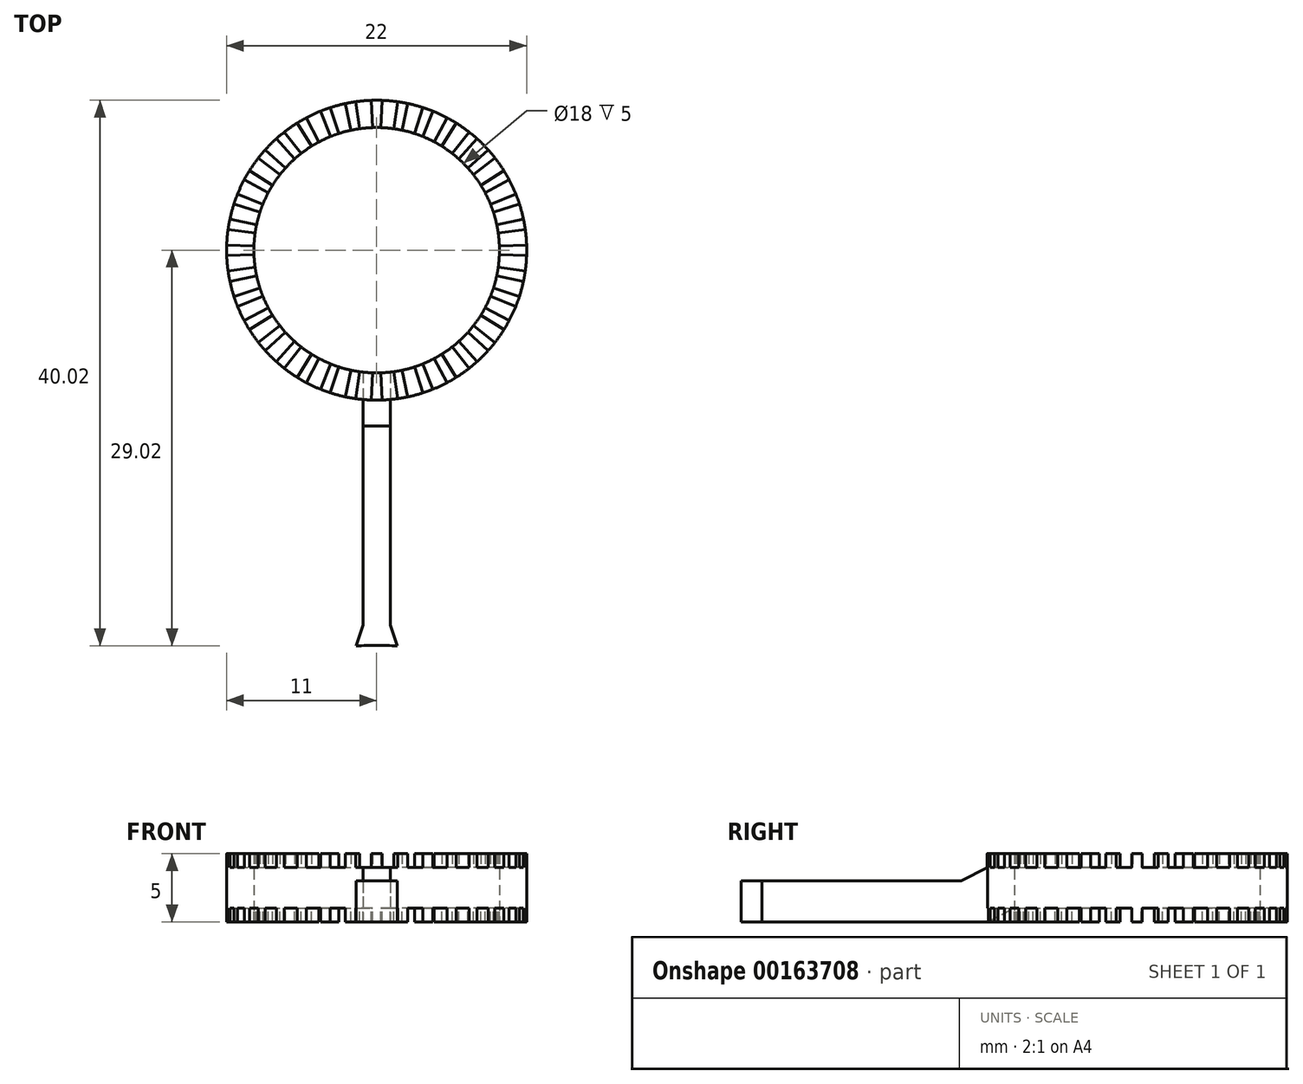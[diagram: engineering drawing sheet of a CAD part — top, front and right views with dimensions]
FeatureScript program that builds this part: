
annotation { "Feature Type Name" : "Feature", "Feature Type Description" : "" }
export const myFeature = defineFeature(function(context is Context, id is Id, definition is map)
    precondition{}
    {
        {
            var Q0;
            Q0=qCreatedBy(makeId("Top.planeOp"),FACE);
            cPlane(context, id + "F0", {"entities" : qUnion([Q0]), "cplaneType" : CPlaneType.OFFSET, "offset" : 1 * mm, "width" : 150 * mm, "height" : 150 * mm});
        }
        {
            var Q0;
            Q0=qCreatedBy(makeId("Top.planeOp"),FACE);
            var sketch = newSketch(context, id + "F1", { "sketchPlane" : qUnion([Q0])});
            skLineSegment(sketch, "E0", {"start": v(-1.5, -20.02) * mm, "end": v(-1, -18.51) * mm});
            skLineSegment(sketch, "E1", {"start": v(-1, -18.51) * mm, "end": v(-1, -1.95) * mm});
            skArc(sketch, "E2", {"start": v(1.5, -20.02) * mm, "mid": v(0, -20) * mm, "end": v(-1.5, -20.02) * mm});
            skLineSegment(sketch, "E3", {"start": v(0, 20) * mm, "end": v(0, -20) * mm, "construction": true});
            skLineSegment(sketch, "E4.MirrorCS", {"start": v(1, -18.51) * mm, "end": v(1, -1.95) * mm});
            skLineSegment(sketch, "E5.MirrorCS", {"start": v(1.5, -20.02) * mm, "end": v(1, -18.51) * mm});
            skLineSegment(sketch, "E6", {"start": v(-1, -1.95) * mm, "end": v(1, -1.95) * mm});
            skSolve(sketch);
        }
        {
            var Q0;
            Q0=qSketchRegion(id+"F1",true);
            extrude(context, id + "F2", {"entities" : qUnion([Q0]), "depth" : 3 * mm});
        }
        {
            var Q0;
            Q0=qCreatedBy(id+"F0.planeOp",FACE);
            var sketch = newSketch(context, id + "F3", { "sketchPlane" : qUnion([Q0])});
            skCircle(sketch, "E7", {"center": v(0, 9) * mm, "radius": 11 * mm});
            skCircle(sketch, "E8", {"center": v(0, 9) * mm, "radius": 9 * mm});
            skSolve(sketch);
        }
        {
            var Q0;
            Q0=qSketchRegion(id+"F3",true);
            extrude(context, id + "F4", {"entities" : qUnion([Q0]), "operationType" : NewBodyOperationType.ADD, "depth" : 3 * mm});
        }
        {
            var Q0;
            Q0=qCreatedBy(makeId("Right.planeOp"),FACE);
            var sketch = newSketch(context, id + "F5", { "sketchPlane" : qUnion([Q0])});
            skLineSegment(sketch, "E9", {"start": v(-1.95, 4) * mm, "end": v(-3.9, 3) * mm});
            skLineSegment(sketch, "E10", {"start": v(-3.9, 3) * mm, "end": v(-1.95, 3) * mm});
            skLineSegment(sketch, "E11", {"start": v(-1.95, 3) * mm, "end": v(-1.95, 4) * mm});
            skLineSegment(sketch, "E12", {"start": v(-1.95, 1) * mm, "end": v(-1.95, 0) * mm});
            skLineSegment(sketch, "E13", {"start": v(-1.95, 0) * mm, "end": v(0, 1) * mm});
            skLineSegment(sketch, "E14", {"start": v(0, 1) * mm, "end": v(-1.95, 1) * mm});
            skLineSegment(sketch, "E15", {"start": v(9, 1) * mm, "end": v(0, 1) * mm, "construction": true});
            skSolve(sketch);
        }
        {
            var Q0;
            Q0=qSketchRegion(id+"F5",true);
            extrude(context, id + "F6", {"entities" : qUnion([Q0]), "operationType" : NewBodyOperationType.ADD, "endBound" : BoundingType.SYMMETRIC, "depth" : 2 * mm});
        }
        {
            var Q0;
            Q0=makeQuery(id+"F4.opExtrude","CAP_FACE",FACE,{"disambiguationData":[OSD([sQuery(id+"F3.wireOp",EDGE,"E7"),sQuery(id+"F3.wireOp",EDGE,"E8")])],"isStart":false});
            var sketch = newSketch(context, id + "F7", { "sketchPlane" : qUnion([Q0])});
            skLineSegment(sketch, "E16", {"start": v(0, 9) * mm, "end": v(0, 20.9) * mm, "construction": true});
            skPoint(sketch, "E16.endSnap0", {"position": v(0, 20) * mm});
            skLineSegment(sketch, "E17", {"start": v(-0.38, 20) * mm, "end": v(-0.31, 18) * mm});
            skArc(sketch, "E18", {"start": v(-0.31, 18) * mm, "mid": v(-0.16, 18) * mm, "end": v(0, 18) * mm});
            skArc(sketch, "E19", {"start": v(-0.38, 20) * mm, "mid": v(-0.2, 20) * mm, "end": v(0, 20) * mm});
            skArc(sketch, "E20.MirrorCS", {"start": v(0.38, 20) * mm, "mid": v(0.2, 20) * mm, "end": v(0, 20) * mm});
            skLineSegment(sketch, "E21.MirrorCS", {"start": v(0.38, 20) * mm, "end": v(0.31, 18) * mm});
            skArc(sketch, "E22.MirrorCS", {"start": v(0.31, 18) * mm, "mid": v(0.16, 18) * mm, "end": v(0, 18) * mm});
            skLineSegment(sketch, "E23.1.0", {"start": v(-2.29, 19.76) * mm, "end": v(-1.87, 17.8) * mm});
            skArc(sketch, "E23.1.1", {"start": v(-2.29, 19.76) * mm, "mid": v(-2.1, 19.8) * mm, "end": v(-1.91, 19.83) * mm});
            skArc(sketch, "E23.1.2", {"start": v(-1.53, 19.9) * mm, "mid": v(-1.72, 19.86) * mm, "end": v(-1.91, 19.83) * mm});
            skLineSegment(sketch, "E23.1.3", {"start": v(-1.53, 19.9) * mm, "end": v(-1.25, 17.91) * mm});
            skArc(sketch, "E23.1.4", {"start": v(-1.25, 17.91) * mm, "mid": v(-1.4, 17.89) * mm, "end": v(-1.56, 17.86) * mm});
            skArc(sketch, "E23.1.5", {"start": v(-1.87, 17.8) * mm, "mid": v(-1.72, 17.83) * mm, "end": v(-1.56, 17.86) * mm});
            skLineSegment(sketch, "E23.2.0", {"start": v(-4.12, 19.2) * mm, "end": v(-3.37, 17.34) * mm});
            skArc(sketch, "E23.2.1", {"start": v(-4.12, 19.2) * mm, "mid": v(-3.94, 19.27) * mm, "end": v(-3.76, 19.34) * mm});
            skArc(sketch, "E23.2.2", {"start": v(-3.4, 19.46) * mm, "mid": v(-3.58, 19.4) * mm, "end": v(-3.76, 19.34) * mm});
            skLineSegment(sketch, "E23.2.3", {"start": v(-3.4, 19.46) * mm, "end": v(-2.78, 17.56) * mm});
            skArc(sketch, "E23.2.4", {"start": v(-2.78, 17.56) * mm, "mid": v(-2.93, 17.5) * mm, "end": v(-3.08, 17.46) * mm});
            skArc(sketch, "E23.2.5", {"start": v(-3.37, 17.34) * mm, "mid": v(-3.23, 17.4) * mm, "end": v(-3.08, 17.46) * mm});
            skLineSegment(sketch, "E23.3.0", {"start": v(-5.83, 18.33) * mm, "end": v(-4.77, 16.63) * mm});
            skArc(sketch, "E23.3.1", {"start": v(-5.83, 18.33) * mm, "mid": v(-5.67, 18.43) * mm, "end": v(-5.5, 18.53) * mm});
            skArc(sketch, "E23.3.2", {"start": v(-5.16, 18.71) * mm, "mid": v(-5.33, 18.62) * mm, "end": v(-5.5, 18.53) * mm});
            skLineSegment(sketch, "E23.3.3", {"start": v(-5.16, 18.71) * mm, "end": v(-4.23, 16.95) * mm});
            skArc(sketch, "E23.3.4", {"start": v(-4.23, 16.95) * mm, "mid": v(-4.36, 16.87) * mm, "end": v(-4.5, 16.8) * mm});
            skArc(sketch, "E23.3.5", {"start": v(-4.77, 16.63) * mm, "mid": v(-4.64, 16.71) * mm, "end": v(-4.5, 16.8) * mm});
            skLineSegment(sketch, "E23.4.0", {"start": v(-7.36, 17.17) * mm, "end": v(-6.02, 15.69) * mm});
            skArc(sketch, "E23.4.1", {"start": v(-7.36, 17.17) * mm, "mid": v(-7.22, 17.3) * mm, "end": v(-7.07, 17.43) * mm});
            skArc(sketch, "E23.4.2", {"start": v(-6.77, 17.67) * mm, "mid": v(-6.92, 17.55) * mm, "end": v(-7.07, 17.43) * mm});
            skLineSegment(sketch, "E23.4.3", {"start": v(-6.77, 17.67) * mm, "end": v(-5.54, 16.1) * mm});
            skArc(sketch, "E23.4.4", {"start": v(-5.54, 16.1) * mm, "mid": v(-5.66, 16) * mm, "end": v(-5.79, 15.9) * mm});
            skArc(sketch, "E23.4.5", {"start": v(-6.02, 15.69) * mm, "mid": v(-5.9, 15.8) * mm, "end": v(-5.79, 15.9) * mm});
            skLineSegment(sketch, "E23.5.0", {"start": v(-8.67, 15.77) * mm, "end": v(-7.1, 14.54) * mm});
            skArc(sketch, "E23.5.1", {"start": v(-8.67, 15.77) * mm, "mid": v(-8.55, 15.92) * mm, "end": v(-8.43, 16.07) * mm});
            skArc(sketch, "E23.5.2", {"start": v(-8.17, 16.36) * mm, "mid": v(-8.3, 16.22) * mm, "end": v(-8.43, 16.07) * mm});
            skLineSegment(sketch, "E23.5.3", {"start": v(-8.17, 16.36) * mm, "end": v(-6.69, 15.02) * mm});
            skArc(sketch, "E23.5.4", {"start": v(-6.69, 15.02) * mm, "mid": v(-6.8, 14.9) * mm, "end": v(-6.9, 14.79) * mm});
            skArc(sketch, "E23.5.5", {"start": v(-7.1, 14.54) * mm, "mid": v(-7, 14.66) * mm, "end": v(-6.9, 14.79) * mm});
            skLineSegment(sketch, "E23.6.0", {"start": v(-9.71, 14.16) * mm, "end": v(-7.95, 13.23) * mm});
            skArc(sketch, "E23.6.1", {"start": v(-9.71, 14.16) * mm, "mid": v(-9.62, 14.33) * mm, "end": v(-9.53, 14.5) * mm});
            skArc(sketch, "E23.6.2", {"start": v(-9.33, 14.83) * mm, "mid": v(-9.43, 14.67) * mm, "end": v(-9.53, 14.5) * mm});
            skLineSegment(sketch, "E23.6.3", {"start": v(-9.33, 14.83) * mm, "end": v(-7.63, 13.77) * mm});
            skArc(sketch, "E23.6.4", {"start": v(-7.63, 13.77) * mm, "mid": v(-7.71, 13.64) * mm, "end": v(-7.8, 13.5) * mm});
            skArc(sketch, "E23.6.5", {"start": v(-7.95, 13.23) * mm, "mid": v(-7.87, 13.36) * mm, "end": v(-7.8, 13.5) * mm});
            skLineSegment(sketch, "E23.7.0", {"start": v(-10.46, 12.4) * mm, "end": v(-8.56, 11.78) * mm});
            skArc(sketch, "E23.7.1", {"start": v(-10.46, 12.4) * mm, "mid": v(-10.4, 12.58) * mm, "end": v(-10.34, 12.76) * mm});
            skArc(sketch, "E23.7.2", {"start": v(-10.2, 13.12) * mm, "mid": v(-10.27, 12.94) * mm, "end": v(-10.34, 12.76) * mm});
            skLineSegment(sketch, "E23.7.3", {"start": v(-10.2, 13.12) * mm, "end": v(-8.34, 12.37) * mm});
            skArc(sketch, "E23.7.4", {"start": v(-8.34, 12.37) * mm, "mid": v(-8.4, 12.23) * mm, "end": v(-8.46, 12.08) * mm});
            skArc(sketch, "E23.7.5", {"start": v(-8.56, 11.78) * mm, "mid": v(-8.5, 11.93) * mm, "end": v(-8.46, 12.08) * mm});
            skLineSegment(sketch, "E23.8.0", {"start": v(-10.9, 10.53) * mm, "end": v(-8.91, 10.25) * mm});
            skArc(sketch, "E23.8.1", {"start": v(-10.9, 10.53) * mm, "mid": v(-10.86, 10.72) * mm, "end": v(-10.83, 10.91) * mm});
            skArc(sketch, "E23.8.2", {"start": v(-10.76, 11.29) * mm, "mid": v(-10.8, 11.1) * mm, "end": v(-10.83, 10.91) * mm});
            skLineSegment(sketch, "E23.8.3", {"start": v(-10.76, 11.29) * mm, "end": v(-8.8, 10.87) * mm});
            skArc(sketch, "E23.8.4", {"start": v(-8.8, 10.87) * mm, "mid": v(-8.83, 10.72) * mm, "end": v(-8.86, 10.56) * mm});
            skArc(sketch, "E23.8.5", {"start": v(-8.91, 10.25) * mm, "mid": v(-8.89, 10.4) * mm, "end": v(-8.86, 10.56) * mm});
            skLineSegment(sketch, "E23.9.0", {"start": v(-11, 8.62) * mm, "end": v(-9, 8.69) * mm});
            skArc(sketch, "E23.9.1", {"start": v(-11, 8.62) * mm, "mid": v(-11, 8.8) * mm, "end": v(-11, 9) * mm});
            skArc(sketch, "E23.9.2", {"start": v(-11, 9.38) * mm, "mid": v(-11, 9.2) * mm, "end": v(-11, 9) * mm});
            skLineSegment(sketch, "E23.9.3", {"start": v(-11, 9.38) * mm, "end": v(-9, 9.31) * mm});
            skArc(sketch, "E23.9.4", {"start": v(-9, 9.31) * mm, "mid": v(-9, 9.16) * mm, "end": v(-9, 9) * mm});
            skArc(sketch, "E23.9.5", {"start": v(-9, 8.69) * mm, "mid": v(-9, 8.84) * mm, "end": v(-9, 9) * mm});
            skLineSegment(sketch, "E23.10.0", {"start": v(-10.76, 6.71) * mm, "end": v(-8.8, 7.13) * mm});
            skArc(sketch, "E23.10.1", {"start": v(-10.76, 6.71) * mm, "mid": v(-10.8, 6.9) * mm, "end": v(-10.83, 7.09) * mm});
            skArc(sketch, "E23.10.2", {"start": v(-10.9, 7.47) * mm, "mid": v(-10.86, 7.28) * mm, "end": v(-10.83, 7.09) * mm});
            skLineSegment(sketch, "E23.10.3", {"start": v(-10.9, 7.47) * mm, "end": v(-8.91, 7.75) * mm});
            skArc(sketch, "E23.10.4", {"start": v(-8.91, 7.75) * mm, "mid": v(-8.89, 7.6) * mm, "end": v(-8.86, 7.44) * mm});
            skArc(sketch, "E23.10.5", {"start": v(-8.8, 7.13) * mm, "mid": v(-8.83, 7.28) * mm, "end": v(-8.86, 7.44) * mm});
            skLineSegment(sketch, "E23.11.0", {"start": v(-10.2, 4.88) * mm, "end": v(-8.34, 5.63) * mm});
            skArc(sketch, "E23.11.1", {"start": v(-10.2, 4.88) * mm, "mid": v(-10.27, 5.06) * mm, "end": v(-10.34, 5.24) * mm});
            skArc(sketch, "E23.11.2", {"start": v(-10.46, 5.6) * mm, "mid": v(-10.4, 5.42) * mm, "end": v(-10.34, 5.24) * mm});
            skLineSegment(sketch, "E23.11.3", {"start": v(-10.46, 5.6) * mm, "end": v(-8.56, 6.22) * mm});
            skArc(sketch, "E23.11.4", {"start": v(-8.56, 6.22) * mm, "mid": v(-8.5, 6.07) * mm, "end": v(-8.46, 5.92) * mm});
            skArc(sketch, "E23.11.5", {"start": v(-8.34, 5.63) * mm, "mid": v(-8.4, 5.77) * mm, "end": v(-8.46, 5.92) * mm});
            skLineSegment(sketch, "E23.12.0", {"start": v(-9.33, 3.17) * mm, "end": v(-7.63, 4.23) * mm});
            skArc(sketch, "E23.12.1", {"start": v(-9.33, 3.17) * mm, "mid": v(-9.43, 3.33) * mm, "end": v(-9.53, 3.5) * mm});
            skArc(sketch, "E23.12.2", {"start": v(-9.71, 3.84) * mm, "mid": v(-9.62, 3.67) * mm, "end": v(-9.53, 3.5) * mm});
            skLineSegment(sketch, "E23.12.3", {"start": v(-9.71, 3.84) * mm, "end": v(-7.95, 4.77) * mm});
            skArc(sketch, "E23.12.4", {"start": v(-7.95, 4.77) * mm, "mid": v(-7.87, 4.64) * mm, "end": v(-7.8, 4.5) * mm});
            skArc(sketch, "E23.12.5", {"start": v(-7.63, 4.23) * mm, "mid": v(-7.71, 4.36) * mm, "end": v(-7.8, 4.5) * mm});
            skLineSegment(sketch, "E23.13.0", {"start": v(-8.17, 1.64) * mm, "end": v(-6.69, 2.98) * mm});
            skArc(sketch, "E23.13.1", {"start": v(-8.17, 1.64) * mm, "mid": v(-8.3, 1.78) * mm, "end": v(-8.43, 1.93) * mm});
            skArc(sketch, "E23.13.2", {"start": v(-8.67, 2.23) * mm, "mid": v(-8.55, 2.08) * mm, "end": v(-8.43, 1.93) * mm});
            skLineSegment(sketch, "E23.13.3", {"start": v(-8.67, 2.23) * mm, "end": v(-7.1, 3.46) * mm});
            skArc(sketch, "E23.13.4", {"start": v(-7.1, 3.46) * mm, "mid": v(-7, 3.34) * mm, "end": v(-6.9, 3.21) * mm});
            skArc(sketch, "E23.13.5", {"start": v(-6.69, 2.98) * mm, "mid": v(-6.8, 3.1) * mm, "end": v(-6.9, 3.21) * mm});
            skLineSegment(sketch, "E23.14.0", {"start": v(-6.77, 0.33) * mm, "end": v(-5.54, 1.9) * mm});
            skArc(sketch, "E23.14.1", {"start": v(-6.77, 0.33) * mm, "mid": v(-6.92, 0.45) * mm, "end": v(-7.07, 0.57) * mm});
            skArc(sketch, "E23.14.2", {"start": v(-7.36, 0.83) * mm, "mid": v(-7.22, 0.7) * mm, "end": v(-7.07, 0.57) * mm});
            skLineSegment(sketch, "E23.14.3", {"start": v(-7.36, 0.83) * mm, "end": v(-6.02, 2.31) * mm});
            skArc(sketch, "E23.14.4", {"start": v(-6.02, 2.31) * mm, "mid": v(-5.9, 2.2) * mm, "end": v(-5.79, 2.1) * mm});
            skArc(sketch, "E23.14.5", {"start": v(-5.54, 1.9) * mm, "mid": v(-5.66, 2) * mm, "end": v(-5.79, 2.1) * mm});
            skLineSegment(sketch, "E23.15.0", {"start": v(-5.16, -0.71) * mm, "end": v(-4.23, 1.05) * mm});
            skArc(sketch, "E23.15.1", {"start": v(-5.16, -0.71) * mm, "mid": v(-5.33, -0.62) * mm, "end": v(-5.5, -0.53) * mm});
            skArc(sketch, "E23.15.2", {"start": v(-5.83, -0.33) * mm, "mid": v(-5.67, -0.43) * mm, "end": v(-5.5, -0.53) * mm});
            skLineSegment(sketch, "E23.15.3", {"start": v(-5.83, -0.33) * mm, "end": v(-4.77, 1.37) * mm});
            skArc(sketch, "E23.15.4", {"start": v(-4.77, 1.37) * mm, "mid": v(-4.64, 1.29) * mm, "end": v(-4.5, 1.2) * mm});
            skArc(sketch, "E23.15.5", {"start": v(-4.23, 1.05) * mm, "mid": v(-4.36, 1.13) * mm, "end": v(-4.5, 1.2) * mm});
            skLineSegment(sketch, "E23.16.0", {"start": v(-3.4, -1.46) * mm, "end": v(-2.78, 0.44) * mm});
            skArc(sketch, "E23.16.1", {"start": v(-3.4, -1.46) * mm, "mid": v(-3.58, -1.4) * mm, "end": v(-3.76, -1.34) * mm});
            skArc(sketch, "E23.16.2", {"start": v(-4.12, -1.2) * mm, "mid": v(-3.94, -1.27) * mm, "end": v(-3.76, -1.34) * mm});
            skLineSegment(sketch, "E23.16.3", {"start": v(-4.12, -1.2) * mm, "end": v(-3.37, 0.66) * mm});
            skArc(sketch, "E23.16.4", {"start": v(-3.37, 0.66) * mm, "mid": v(-3.23, 0.6) * mm, "end": v(-3.08, 0.54) * mm});
            skArc(sketch, "E23.16.5", {"start": v(-2.78, 0.44) * mm, "mid": v(-2.93, 0.5) * mm, "end": v(-3.08, 0.54) * mm});
            skLineSegment(sketch, "E23.17.0", {"start": v(-1.53, -1.9) * mm, "end": v(-1.25, 0.09) * mm});
            skArc(sketch, "E23.17.1", {"start": v(-1.53, -1.9) * mm, "mid": v(-1.72, -1.86) * mm, "end": v(-1.91, -1.83) * mm});
            skArc(sketch, "E23.17.2", {"start": v(-2.29, -1.76) * mm, "mid": v(-2.1, -1.8) * mm, "end": v(-1.91, -1.83) * mm});
            skLineSegment(sketch, "E23.17.3", {"start": v(-2.29, -1.76) * mm, "end": v(-1.87, 0.2) * mm});
            skArc(sketch, "E23.17.4", {"start": v(-1.87, 0.2) * mm, "mid": v(-1.72, 0.17) * mm, "end": v(-1.56, 0.14) * mm});
            skArc(sketch, "E23.17.5", {"start": v(-1.25, 0.09) * mm, "mid": v(-1.4, 0.11) * mm, "end": v(-1.56, 0.14) * mm});
            skLineSegment(sketch, "E23.18.0", {"start": v(0.38, -2) * mm, "end": v(0.31, 0) * mm});
            skArc(sketch, "E23.18.1", {"start": v(0.38, -2) * mm, "mid": v(0.2, -2) * mm, "end": v(0, -2) * mm});
            skArc(sketch, "E23.18.2", {"start": v(-0.38, -2) * mm, "mid": v(-0.2, -2) * mm, "end": v(0, -2) * mm});
            skLineSegment(sketch, "E23.18.3", {"start": v(-0.38, -2) * mm, "end": v(-0.31, 0) * mm});
            skArc(sketch, "E23.18.4", {"start": v(-0.31, 0) * mm, "mid": v(-0.16, 0) * mm, "end": v(0, 0) * mm});
            skArc(sketch, "E23.18.5", {"start": v(0.31, 0) * mm, "mid": v(0.16, 0) * mm, "end": v(0, 0) * mm});
            skLineSegment(sketch, "E23.19.0", {"start": v(2.29, -1.76) * mm, "end": v(1.87, 0.2) * mm});
            skArc(sketch, "E23.19.1", {"start": v(2.29, -1.76) * mm, "mid": v(2.1, -1.8) * mm, "end": v(1.91, -1.83) * mm});
            skArc(sketch, "E23.19.2", {"start": v(1.53, -1.9) * mm, "mid": v(1.72, -1.86) * mm, "end": v(1.91, -1.83) * mm});
            skLineSegment(sketch, "E23.19.3", {"start": v(1.53, -1.9) * mm, "end": v(1.25, 0.09) * mm});
            skArc(sketch, "E23.19.4", {"start": v(1.25, 0.09) * mm, "mid": v(1.4, 0.11) * mm, "end": v(1.56, 0.14) * mm});
            skArc(sketch, "E23.19.5", {"start": v(1.87, 0.2) * mm, "mid": v(1.72, 0.17) * mm, "end": v(1.56, 0.14) * mm});
            skLineSegment(sketch, "E23.20.0", {"start": v(4.12, -1.2) * mm, "end": v(3.37, 0.66) * mm});
            skArc(sketch, "E23.20.1", {"start": v(4.12, -1.2) * mm, "mid": v(3.94, -1.27) * mm, "end": v(3.76, -1.34) * mm});
            skArc(sketch, "E23.20.2", {"start": v(3.4, -1.46) * mm, "mid": v(3.58, -1.4) * mm, "end": v(3.76, -1.34) * mm});
            skLineSegment(sketch, "E23.20.3", {"start": v(3.4, -1.46) * mm, "end": v(2.78, 0.44) * mm});
            skArc(sketch, "E23.20.4", {"start": v(2.78, 0.44) * mm, "mid": v(2.93, 0.5) * mm, "end": v(3.08, 0.54) * mm});
            skArc(sketch, "E23.20.5", {"start": v(3.37, 0.66) * mm, "mid": v(3.23, 0.6) * mm, "end": v(3.08, 0.54) * mm});
            skLineSegment(sketch, "E23.21.0", {"start": v(5.83, -0.33) * mm, "end": v(4.77, 1.37) * mm});
            skArc(sketch, "E23.21.1", {"start": v(5.83, -0.33) * mm, "mid": v(5.67, -0.43) * mm, "end": v(5.5, -0.53) * mm});
            skArc(sketch, "E23.21.2", {"start": v(5.16, -0.71) * mm, "mid": v(5.33, -0.62) * mm, "end": v(5.5, -0.53) * mm});
            skLineSegment(sketch, "E23.21.3", {"start": v(5.16, -0.71) * mm, "end": v(4.23, 1.05) * mm});
            skArc(sketch, "E23.21.4", {"start": v(4.23, 1.05) * mm, "mid": v(4.36, 1.13) * mm, "end": v(4.5, 1.2) * mm});
            skArc(sketch, "E23.21.5", {"start": v(4.77, 1.37) * mm, "mid": v(4.64, 1.29) * mm, "end": v(4.5, 1.2) * mm});
            skLineSegment(sketch, "E23.22.0", {"start": v(7.36, 0.83) * mm, "end": v(6.02, 2.31) * mm});
            skArc(sketch, "E23.22.1", {"start": v(7.36, 0.83) * mm, "mid": v(7.22, 0.7) * mm, "end": v(7.07, 0.57) * mm});
            skArc(sketch, "E23.22.2", {"start": v(6.77, 0.33) * mm, "mid": v(6.92, 0.45) * mm, "end": v(7.07, 0.57) * mm});
            skLineSegment(sketch, "E23.22.3", {"start": v(6.77, 0.33) * mm, "end": v(5.54, 1.9) * mm});
            skArc(sketch, "E23.22.4", {"start": v(5.54, 1.9) * mm, "mid": v(5.66, 2) * mm, "end": v(5.79, 2.1) * mm});
            skArc(sketch, "E23.22.5", {"start": v(6.02, 2.31) * mm, "mid": v(5.9, 2.2) * mm, "end": v(5.79, 2.1) * mm});
            skLineSegment(sketch, "E23.23.0", {"start": v(8.67, 2.23) * mm, "end": v(7.1, 3.46) * mm});
            skArc(sketch, "E23.23.1", {"start": v(8.67, 2.23) * mm, "mid": v(8.55, 2.08) * mm, "end": v(8.43, 1.93) * mm});
            skArc(sketch, "E23.23.2", {"start": v(8.17, 1.64) * mm, "mid": v(8.3, 1.78) * mm, "end": v(8.43, 1.93) * mm});
            skLineSegment(sketch, "E23.23.3", {"start": v(8.17, 1.64) * mm, "end": v(6.69, 2.98) * mm});
            skArc(sketch, "E23.23.4", {"start": v(6.69, 2.98) * mm, "mid": v(6.8, 3.1) * mm, "end": v(6.9, 3.21) * mm});
            skArc(sketch, "E23.23.5", {"start": v(7.1, 3.46) * mm, "mid": v(7, 3.34) * mm, "end": v(6.9, 3.21) * mm});
            skLineSegment(sketch, "E23.24.0", {"start": v(9.71, 3.84) * mm, "end": v(7.95, 4.77) * mm});
            skArc(sketch, "E23.24.1", {"start": v(9.71, 3.84) * mm, "mid": v(9.62, 3.67) * mm, "end": v(9.53, 3.5) * mm});
            skArc(sketch, "E23.24.2", {"start": v(9.33, 3.17) * mm, "mid": v(9.43, 3.33) * mm, "end": v(9.53, 3.5) * mm});
            skLineSegment(sketch, "E23.24.3", {"start": v(9.33, 3.17) * mm, "end": v(7.63, 4.23) * mm});
            skArc(sketch, "E23.24.4", {"start": v(7.63, 4.23) * mm, "mid": v(7.71, 4.36) * mm, "end": v(7.8, 4.5) * mm});
            skArc(sketch, "E23.24.5", {"start": v(7.95, 4.77) * mm, "mid": v(7.87, 4.64) * mm, "end": v(7.8, 4.5) * mm});
            skLineSegment(sketch, "E23.25.0", {"start": v(10.46, 5.6) * mm, "end": v(8.56, 6.22) * mm});
            skArc(sketch, "E23.25.1", {"start": v(10.46, 5.6) * mm, "mid": v(10.4, 5.42) * mm, "end": v(10.34, 5.24) * mm});
            skArc(sketch, "E23.25.2", {"start": v(10.2, 4.88) * mm, "mid": v(10.27, 5.06) * mm, "end": v(10.34, 5.24) * mm});
            skLineSegment(sketch, "E23.25.3", {"start": v(10.2, 4.88) * mm, "end": v(8.34, 5.63) * mm});
            skArc(sketch, "E23.25.4", {"start": v(8.34, 5.63) * mm, "mid": v(8.4, 5.77) * mm, "end": v(8.46, 5.92) * mm});
            skArc(sketch, "E23.25.5", {"start": v(8.56, 6.22) * mm, "mid": v(8.5, 6.07) * mm, "end": v(8.46, 5.92) * mm});
            skLineSegment(sketch, "E23.26.0", {"start": v(10.9, 7.47) * mm, "end": v(8.91, 7.75) * mm});
            skArc(sketch, "E23.26.1", {"start": v(10.9, 7.47) * mm, "mid": v(10.86, 7.28) * mm, "end": v(10.83, 7.09) * mm});
            skArc(sketch, "E23.26.2", {"start": v(10.76, 6.71) * mm, "mid": v(10.8, 6.9) * mm, "end": v(10.83, 7.09) * mm});
            skLineSegment(sketch, "E23.26.3", {"start": v(10.76, 6.71) * mm, "end": v(8.8, 7.13) * mm});
            skArc(sketch, "E23.26.4", {"start": v(8.8, 7.13) * mm, "mid": v(8.83, 7.28) * mm, "end": v(8.86, 7.44) * mm});
            skArc(sketch, "E23.26.5", {"start": v(8.91, 7.75) * mm, "mid": v(8.89, 7.6) * mm, "end": v(8.86, 7.44) * mm});
            skLineSegment(sketch, "E23.27.0", {"start": v(11, 9.38) * mm, "end": v(9, 9.31) * mm});
            skArc(sketch, "E23.27.1", {"start": v(11, 9.38) * mm, "mid": v(11, 9.2) * mm, "end": v(11, 9) * mm});
            skArc(sketch, "E23.27.2", {"start": v(11, 8.62) * mm, "mid": v(11, 8.8) * mm, "end": v(11, 9) * mm});
            skLineSegment(sketch, "E23.27.3", {"start": v(11, 8.62) * mm, "end": v(9, 8.69) * mm});
            skArc(sketch, "E23.27.4", {"start": v(9, 8.69) * mm, "mid": v(9, 8.84) * mm, "end": v(9, 9) * mm});
            skArc(sketch, "E23.27.5", {"start": v(9, 9.31) * mm, "mid": v(9, 9.16) * mm, "end": v(9, 9) * mm});
            skLineSegment(sketch, "E23.28.0", {"start": v(10.76, 11.29) * mm, "end": v(8.8, 10.87) * mm});
            skArc(sketch, "E23.28.1", {"start": v(10.76, 11.29) * mm, "mid": v(10.8, 11.1) * mm, "end": v(10.83, 10.91) * mm});
            skArc(sketch, "E23.28.2", {"start": v(10.9, 10.53) * mm, "mid": v(10.86, 10.72) * mm, "end": v(10.83, 10.91) * mm});
            skLineSegment(sketch, "E23.28.3", {"start": v(10.9, 10.53) * mm, "end": v(8.91, 10.25) * mm});
            skArc(sketch, "E23.28.4", {"start": v(8.91, 10.25) * mm, "mid": v(8.89, 10.4) * mm, "end": v(8.86, 10.56) * mm});
            skArc(sketch, "E23.28.5", {"start": v(8.8, 10.87) * mm, "mid": v(8.83, 10.72) * mm, "end": v(8.86, 10.56) * mm});
            skLineSegment(sketch, "E23.29.0", {"start": v(10.2, 13.12) * mm, "end": v(8.34, 12.37) * mm});
            skArc(sketch, "E23.29.1", {"start": v(10.2, 13.12) * mm, "mid": v(10.27, 12.94) * mm, "end": v(10.34, 12.76) * mm});
            skArc(sketch, "E23.29.2", {"start": v(10.46, 12.4) * mm, "mid": v(10.4, 12.58) * mm, "end": v(10.34, 12.76) * mm});
            skLineSegment(sketch, "E23.29.3", {"start": v(10.46, 12.4) * mm, "end": v(8.56, 11.78) * mm});
            skArc(sketch, "E23.29.4", {"start": v(8.56, 11.78) * mm, "mid": v(8.5, 11.93) * mm, "end": v(8.46, 12.08) * mm});
            skArc(sketch, "E23.29.5", {"start": v(8.34, 12.37) * mm, "mid": v(8.4, 12.23) * mm, "end": v(8.46, 12.08) * mm});
            skLineSegment(sketch, "E23.30.0", {"start": v(9.33, 14.83) * mm, "end": v(7.63, 13.77) * mm});
            skArc(sketch, "E23.30.1", {"start": v(9.33, 14.83) * mm, "mid": v(9.43, 14.67) * mm, "end": v(9.53, 14.5) * mm});
            skArc(sketch, "E23.30.2", {"start": v(9.71, 14.16) * mm, "mid": v(9.62, 14.33) * mm, "end": v(9.53, 14.5) * mm});
            skLineSegment(sketch, "E23.30.3", {"start": v(9.71, 14.16) * mm, "end": v(7.95, 13.23) * mm});
            skArc(sketch, "E23.30.4", {"start": v(7.95, 13.23) * mm, "mid": v(7.87, 13.36) * mm, "end": v(7.8, 13.5) * mm});
            skArc(sketch, "E23.30.5", {"start": v(7.63, 13.77) * mm, "mid": v(7.71, 13.64) * mm, "end": v(7.8, 13.5) * mm});
            skLineSegment(sketch, "E23.31.0", {"start": v(8.17, 16.36) * mm, "end": v(6.69, 15.02) * mm});
            skArc(sketch, "E23.31.1", {"start": v(8.17, 16.36) * mm, "mid": v(8.3, 16.22) * mm, "end": v(8.43, 16.07) * mm});
            skArc(sketch, "E23.31.2", {"start": v(8.67, 15.77) * mm, "mid": v(8.55, 15.92) * mm, "end": v(8.43, 16.07) * mm});
            skLineSegment(sketch, "E23.31.3", {"start": v(8.67, 15.77) * mm, "end": v(7.1, 14.54) * mm});
            skArc(sketch, "E23.31.4", {"start": v(7.1, 14.54) * mm, "mid": v(7, 14.66) * mm, "end": v(6.9, 14.79) * mm});
            skArc(sketch, "E23.31.5", {"start": v(6.69, 15.02) * mm, "mid": v(6.8, 14.9) * mm, "end": v(6.9, 14.79) * mm});
            skLineSegment(sketch, "E23.32.0", {"start": v(6.77, 17.67) * mm, "end": v(5.54, 16.1) * mm});
            skArc(sketch, "E23.32.1", {"start": v(6.77, 17.67) * mm, "mid": v(6.92, 17.55) * mm, "end": v(7.07, 17.43) * mm});
            skArc(sketch, "E23.32.2", {"start": v(7.36, 17.17) * mm, "mid": v(7.22, 17.3) * mm, "end": v(7.07, 17.43) * mm});
            skLineSegment(sketch, "E23.32.3", {"start": v(7.36, 17.17) * mm, "end": v(6.02, 15.69) * mm});
            skArc(sketch, "E23.32.4", {"start": v(6.02, 15.69) * mm, "mid": v(5.9, 15.8) * mm, "end": v(5.79, 15.9) * mm});
            skArc(sketch, "E23.32.5", {"start": v(5.54, 16.1) * mm, "mid": v(5.66, 16) * mm, "end": v(5.79, 15.9) * mm});
            skLineSegment(sketch, "E23.33.0", {"start": v(5.16, 18.71) * mm, "end": v(4.23, 16.95) * mm});
            skArc(sketch, "E23.33.1", {"start": v(5.16, 18.71) * mm, "mid": v(5.33, 18.62) * mm, "end": v(5.5, 18.53) * mm});
            skArc(sketch, "E23.33.2", {"start": v(5.83, 18.33) * mm, "mid": v(5.67, 18.43) * mm, "end": v(5.5, 18.53) * mm});
            skLineSegment(sketch, "E23.33.3", {"start": v(5.83, 18.33) * mm, "end": v(4.77, 16.63) * mm});
            skArc(sketch, "E23.33.4", {"start": v(4.77, 16.63) * mm, "mid": v(4.64, 16.71) * mm, "end": v(4.5, 16.8) * mm});
            skArc(sketch, "E23.33.5", {"start": v(4.23, 16.95) * mm, "mid": v(4.36, 16.87) * mm, "end": v(4.5, 16.8) * mm});
            skLineSegment(sketch, "E23.34.0", {"start": v(3.4, 19.46) * mm, "end": v(2.78, 17.56) * mm});
            skArc(sketch, "E23.34.1", {"start": v(3.4, 19.46) * mm, "mid": v(3.58, 19.4) * mm, "end": v(3.76, 19.34) * mm});
            skArc(sketch, "E23.34.2", {"start": v(4.12, 19.2) * mm, "mid": v(3.94, 19.27) * mm, "end": v(3.76, 19.34) * mm});
            skLineSegment(sketch, "E23.34.3", {"start": v(4.12, 19.2) * mm, "end": v(3.37, 17.34) * mm});
            skArc(sketch, "E23.34.4", {"start": v(3.37, 17.34) * mm, "mid": v(3.23, 17.4) * mm, "end": v(3.08, 17.46) * mm});
            skArc(sketch, "E23.34.5", {"start": v(2.78, 17.56) * mm, "mid": v(2.93, 17.5) * mm, "end": v(3.08, 17.46) * mm});
            skLineSegment(sketch, "E23.35.0", {"start": v(1.53, 19.9) * mm, "end": v(1.25, 17.91) * mm});
            skArc(sketch, "E23.35.1", {"start": v(1.53, 19.9) * mm, "mid": v(1.72, 19.86) * mm, "end": v(1.91, 19.83) * mm});
            skArc(sketch, "E23.35.2", {"start": v(2.29, 19.76) * mm, "mid": v(2.1, 19.8) * mm, "end": v(1.91, 19.83) * mm});
            skLineSegment(sketch, "E23.35.3", {"start": v(2.29, 19.76) * mm, "end": v(1.87, 17.8) * mm});
            skArc(sketch, "E23.35.4", {"start": v(1.87, 17.8) * mm, "mid": v(1.72, 17.83) * mm, "end": v(1.56, 17.86) * mm});
            skArc(sketch, "E23.35.5", {"start": v(1.25, 17.91) * mm, "mid": v(1.4, 17.89) * mm, "end": v(1.56, 17.86) * mm});
            skSolve(sketch);
        }
        {
            var Q0;
            Q0=qSketchRegion(id+"F7",true);
            extrude(context, id + "F8", {"entities" : qUnion([Q0]), "operationType" : NewBodyOperationType.ADD, "depth" : 1 * mm});
        }
        {
            var Q0;
            Q0=qSketchRegion(id+"F7",true);
            extrude(context, id + "F9", {"entities" : qUnion([Q0]), "operationType" : NewBodyOperationType.ADD, "oppositeDirection" : true, "depth" : 4 * mm});
        }
    });
